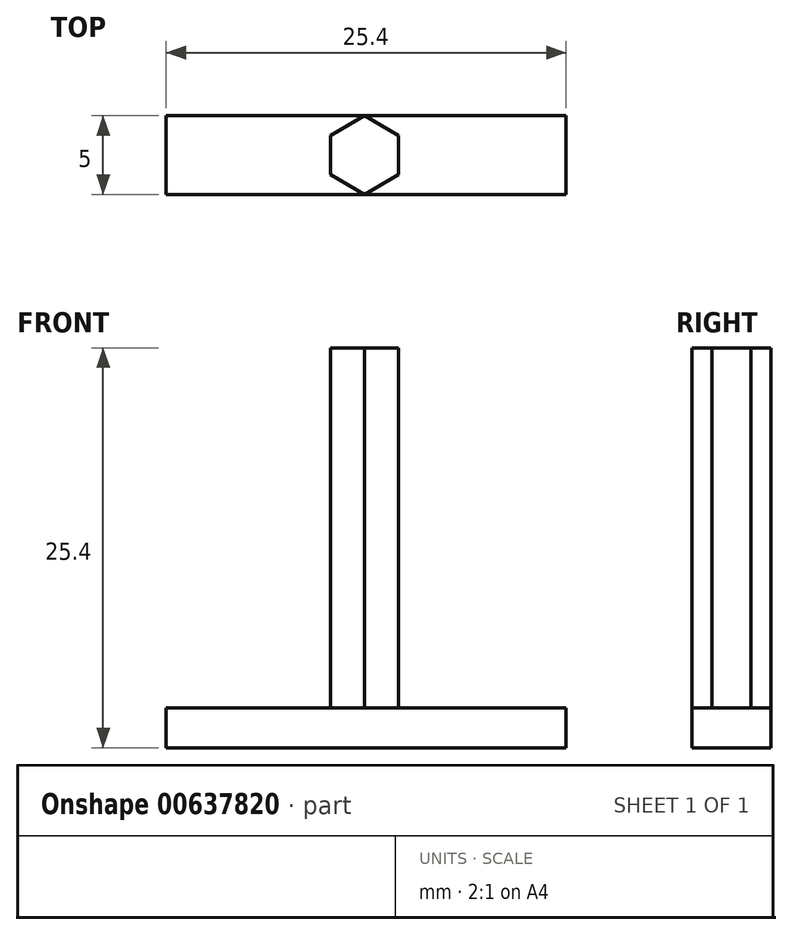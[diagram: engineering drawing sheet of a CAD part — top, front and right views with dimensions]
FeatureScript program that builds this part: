
annotation { "Feature Type Name" : "Feature", "Feature Type Description" : "" }
export const myFeature = defineFeature(function(context is Context, id is Id, definition is map)
    precondition{}
    {
        {
            var Q0;
            Q0=qCreatedBy(makeId("Top.planeOp"),FACE);
            var sketch = newSketch(context, id + "F0", { "sketchPlane" : qUnion([Q0])});
            skLineSegment(sketch, "E0.bottom", {"start": v(-62.12, 31.3) * mm, "end": v(-36.72, 31.3) * mm});
            skLineSegment(sketch, "E0.top", {"start": v(-62.12, 26.3) * mm, "end": v(-36.72, 26.3) * mm});
            skLineSegment(sketch, "E0.left", {"start": v(-62.12, 31.3) * mm, "end": v(-62.12, 26.3) * mm});
            skLineSegment(sketch, "E0.right", {"start": v(-36.72, 31.3) * mm, "end": v(-36.72, 26.3) * mm});
            skLineSegment(sketch, "E1", {"start": v(-51.7, 30.04) * mm, "end": v(-51.7, 27.54) * mm});
            skLineSegment(sketch, "E2", {"start": v(-51.7, 27.54) * mm, "end": v(-49.53, 26.3) * mm});
            skLineSegment(sketch, "E3", {"start": v(-49.53, 26.3) * mm, "end": v(-47.37, 27.54) * mm});
            skLineSegment(sketch, "E4", {"start": v(-47.37, 27.54) * mm, "end": v(-47.37, 30.04) * mm});
            skLineSegment(sketch, "E5", {"start": v(-47.37, 30.04) * mm, "end": v(-49.53, 31.3) * mm});
            skLineSegment(sketch, "E6", {"start": v(-49.53, 31.3) * mm, "end": v(-51.7, 30.04) * mm});
            skSolve(sketch);
        }
        {
            var Q0;
            Q0=makeQuery(id+"F0.imprint","IMPRINT",FACE,{"disambiguationData":[TD([[makeQuery(id+"F0.imprint","IMPRINT",EDGE,{"derivedFrom":sQuery(id+"F0.wireOp",EDGE,"E1")}),1.0]])]});
            extrude(context, id + "F1", {"entities" : qUnion([Q0]), "depth" : 25.4 * mm, "offsetDistance" : 25.4 * mm});
        }
        {
            var Q0;
            Q0 = qSketchRegion(id + "F0", true);
            extrude(context, id + "F2", {"entities" : qUnion([Q0]), "operationType" : NewBodyOperationType.ADD, "depth" : 2.54 * mm, "offsetDistance" : 25.4 * mm});
        }
    });
